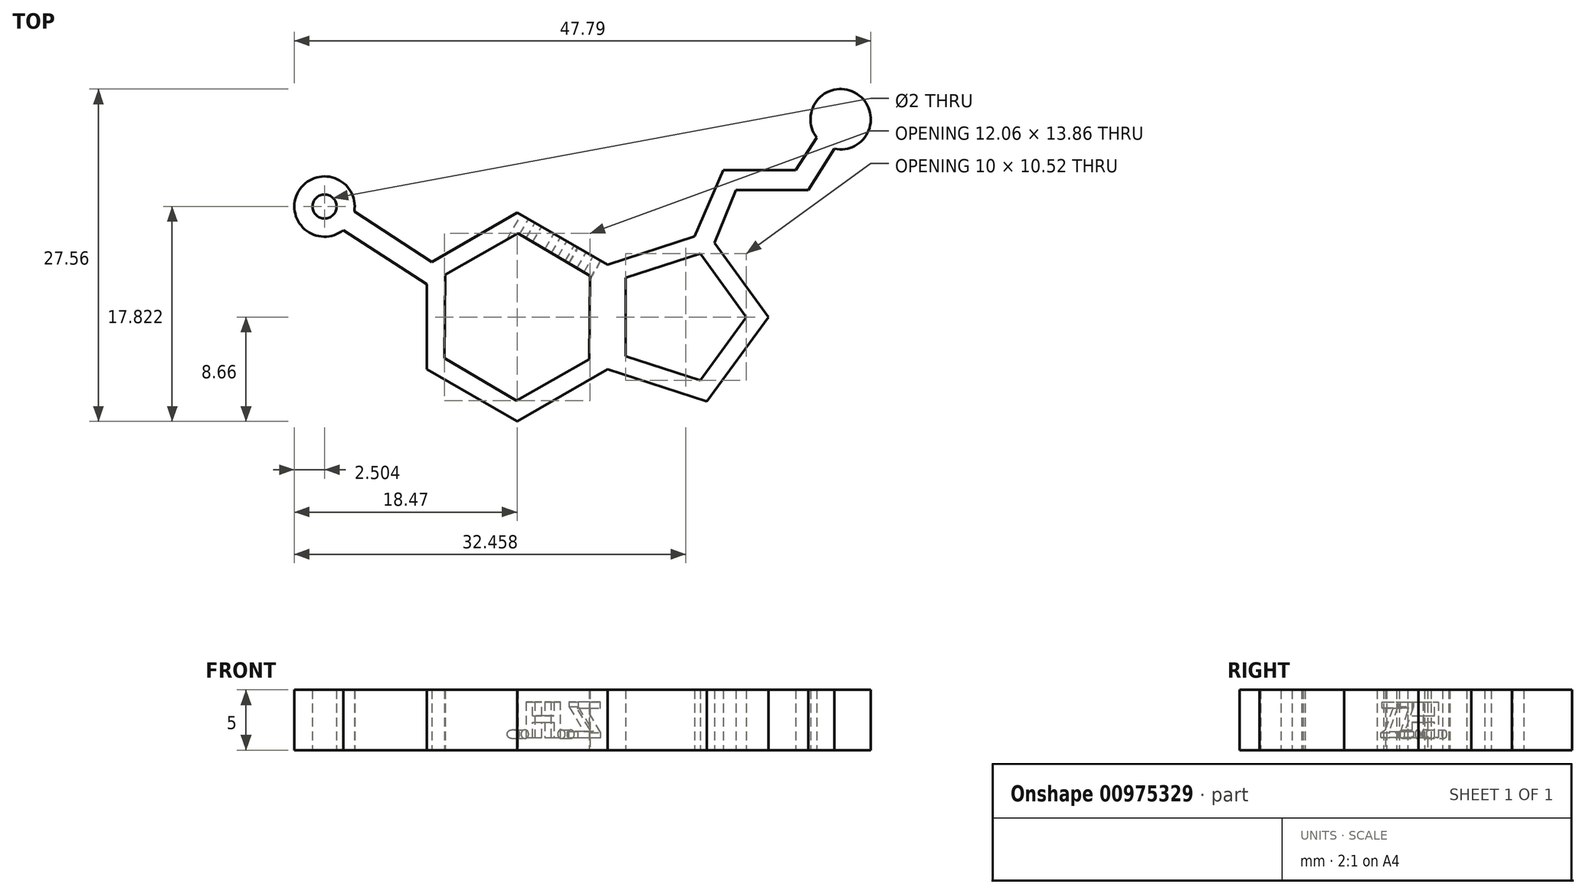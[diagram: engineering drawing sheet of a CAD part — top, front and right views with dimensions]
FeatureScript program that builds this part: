
annotation { "Feature Type Name" : "Feature", "Feature Type Description" : "" }
export const myFeature = defineFeature(function(context is Context, id is Id, definition is map)
    precondition{}
    {
        {
            var Q0;
            Q0=qCreatedBy(makeId("Top.planeOp"),FACE);
            var sketch = newSketch(context, id + "F0", { "sketchPlane" : qUnion([Q0])});
            skCircle(sketch, "E0.cCircle", {"center": v(0, 0) * mm, "radius": 7.5 * mm, "construction": true});
            skLineSegment(sketch, "E0.0", {"start": v(-7.5, 4.33) * mm, "end": v(0, 8.66) * mm});
            skLineSegment(sketch, "E0.1", {"start": v(0, 8.66) * mm, "end": v(7.5, 4.33) * mm});
            skLineSegment(sketch, "E0.2", {"start": v(7.5, 4.33) * mm, "end": v(7.5, -4.33) * mm});
            skLineSegment(sketch, "E0.3", {"start": v(7.5, -4.33) * mm, "end": v(0, -8.66) * mm});
            skLineSegment(sketch, "E0.4", {"start": v(0, -8.66) * mm, "end": v(-7.5, -4.33) * mm});
            skLineSegment(sketch, "E0.5", {"start": v(-7.5, -4.33) * mm, "end": v(-7.5, 4.33) * mm});
            skPoint(sketch, "E0.0.midPoint", {"position": v(-3.75, 6.5) * mm});
            skCircle(sketch, "E1.cCircle", {"center": v(13.46, 0) * mm, "radius": 5.96 * mm, "construction": true});
            skLineSegment(sketch, "E1.0", {"start": v(7.5, 4.33) * mm, "end": v(15.74, 7) * mm});
            skLineSegment(sketch, "E1.1", {"start": v(15.74, 7) * mm, "end": v(20.83, 0) * mm});
            skLineSegment(sketch, "E1.2", {"start": v(20.83, 0) * mm, "end": v(15.74, -7) * mm});
            skLineSegment(sketch, "E1.3", {"start": v(15.74, -7) * mm, "end": v(7.5, -4.33) * mm});
            skLineSegment(sketch, "E1.4", {"start": v(7.5, -4.33) * mm, "end": v(7.5, 4.33) * mm});
            skPoint(sketch, "E1.0.midPoint", {"position": v(11.62, 5.67) * mm});
            skCircle(sketch, "E2.cCircle", {"center": v(0, 0) * mm, "radius": 6 * mm, "construction": true});
            skLineSegment(sketch, "E2.0", {"start": v(0.06, 6.93) * mm, "end": v(6.03, 3.42) * mm});
            skLineSegment(sketch, "E2.1", {"start": v(6.03, 3.42) * mm, "end": v(5.97, -3.51) * mm});
            skLineSegment(sketch, "E2.2", {"start": v(5.97, -3.51) * mm, "end": v(-0.06, -6.93) * mm});
            skLineSegment(sketch, "E2.3", {"start": v(-0.06, -6.93) * mm, "end": v(-6.03, -3.42) * mm});
            skLineSegment(sketch, "E2.4", {"start": v(-6.03, -3.42) * mm, "end": v(-5.97, 3.51) * mm});
            skLineSegment(sketch, "E2.5", {"start": v(-5.97, 3.51) * mm, "end": v(0.06, 6.93) * mm});
            skPoint(sketch, "E2.0.midPoint", {"position": v(3.04, 5.17) * mm});
            skCircle(sketch, "E3.cCircle", {"center": v(13.46, 0) * mm, "radius": 4.47 * mm, "construction": true});
            skLineSegment(sketch, "E3.0", {"start": v(15.17, 5.26) * mm, "end": v(18.99, 0) * mm});
            skLineSegment(sketch, "E3.1", {"start": v(18.99, 0) * mm, "end": v(15.17, -5.26) * mm});
            skLineSegment(sketch, "E3.2", {"start": v(15.17, -5.26) * mm, "end": v(8.99, -3.25) * mm});
            skLineSegment(sketch, "E3.3", {"start": v(8.99, -3.25) * mm, "end": v(8.99, 3.25) * mm});
            skLineSegment(sketch, "E3.4", {"start": v(8.99, 3.25) * mm, "end": v(15.17, 5.26) * mm});
            skPoint(sketch, "E3.0.midPoint", {"position": v(17.08, 2.63) * mm});
            skCircle(sketch, "E4", {"center": v(26.82, 16.4) * mm, "radius": 2.5 * mm});
            skCircle(sketch, "E5", {"center": v(-15.97, 9.16) * mm, "radius": 2.5 * mm});
            skCircle(sketch, "E6", {"center": v(-15.97, 9.16) * mm, "radius": 1 * mm});
            skLineSegment(sketch, "E7", {"start": v(-7.5, 2.71) * mm, "end": v(-15.88, 8.17) * mm});
            skLineSegment(sketch, "E8", {"start": v(-7.08, 4.57) * mm, "end": v(-15.46, 10.02) * mm});
            skLineSegment(sketch, "E9", {"start": v(14.71, 6.67) * mm, "end": v(17.1, 12.18) * mm});
            skLineSegment(sketch, "E10", {"start": v(17.1, 12.18) * mm, "end": v(23.1, 12.18) * mm});
            skLineSegment(sketch, "E11", {"start": v(23.1, 12.18) * mm, "end": v(25.78, 16.4) * mm});
            skLineSegment(sketch, "E12", {"start": v(18.13, 10.52) * mm, "end": v(24.13, 10.52) * mm});
            skLineSegment(sketch, "E13", {"start": v(24.13, 10.52) * mm, "end": v(26.8, 14.74) * mm});
            skLineSegment(sketch, "E14", {"start": v(18.13, 10.52) * mm, "end": v(16.36, 6.15) * mm});
            skSolve(sketch);
        }
        {
            var Q0;
            {var subQ0=sQuery(id+"F0.wireOp",EDGE,"E4");var subQ1=makeQuery(id+"F0.imprint","INTERSECT",VERTEX,{"derivedFrom":[subQ0,sQuery(id+"F0.wireOp",EDGE,"E11")]});Q0=makeQuery(id+"F0.imprint","IMPRINT",FACE,{"disambiguationData":[TD([[makeQuery(id+"F0.imprint","IMPRINT",EDGE,{"disambiguationData":[TD([[subQ1,-1.0]])],"derivedFrom":subQ0}),1.0]])]});}
            var Q1;
            {var subQ0=sQuery(id+"F0.wireOp",EDGE,"E9");Q1=makeQuery(id+"F0.imprint","IMPRINT",FACE,{"disambiguationData":[TD([[makeQuery(id+"F0.imprint","IMPRINT",EDGE,{"derivedFrom":subQ0}),-1.0]])]});}
            var Q2;
            {var subQ6=sQuery(id+"F0.wireOp",EDGE,"E0.1");Q2=makeQuery(id+"F0.imprint","IMPRINT",FACE,{"disambiguationData":[TD([[makeQuery(id+"F0.imprint","IMPRINT",EDGE,{"derivedFrom":subQ6}),-1.0]])]});}
            var Q3;
            {var subQ1=sQuery(id+"F0.wireOp",EDGE,"E1.2");Q3=makeQuery(id+"F0.imprint","IMPRINT",FACE,{"disambiguationData":[TD([[makeQuery(id+"F0.imprint","IMPRINT",EDGE,{"derivedFrom":subQ1}),-1.0]])]});}
            var Q4;
            {var subQ0=sQuery(id+"F0.wireOp",EDGE,"E7");var subQ1=sQuery(id+"F0.wireOp",EDGE,"E5");var subQ2=makeQuery(id+"F0.imprint","INTERSECT",VERTEX,{"derivedFrom":[subQ1,subQ0]});Q4=makeQuery(id+"F0.imprint","IMPRINT",FACE,{"disambiguationData":[TD([[makeQuery(id+"F0.imprint","IMPRINT",EDGE,{"disambiguationData":[TD([[subQ2,-1.0]])],"derivedFrom":subQ1}),1.0]])]});}
            var Q5;
            {var subQ0=sQuery(id+"F0.wireOp",EDGE,"E7");var subQ6=sQuery(id+"F0.wireOp",EDGE,"E5");var subQ7=makeQuery(id+"F0.imprint","INTERSECT",VERTEX,{"derivedFrom":[subQ6,subQ0]});Q5=makeQuery(id+"F0.imprint","IMPRINT",FACE,{"disambiguationData":[TD([[makeQuery(id+"F0.imprint","IMPRINT",EDGE,{"disambiguationData":[TD([[subQ7,1.0]])],"derivedFrom":subQ6}),1.0]])]});}
            var Q6;
            {var subQ1=sQuery(id+"F0.wireOp",EDGE,"E0.5");var subQ7=sQuery(id+"F0.wireOp",EDGE,"E0.0");var subQ8=makeQuery(id+"F0.imprint","INTERSECT",VERTEX,{"derivedFrom":[subQ7,subQ1]});Q6=makeQuery(id+"F0.imprint","IMPRINT",FACE,{"disambiguationData":[TD([[makeQuery(id+"F0.imprint","IMPRINT",EDGE,{"disambiguationData":[TD([[subQ8,-1.0]])],"derivedFrom":subQ7}),1.0]])]});}
            extrude(context, id + "F1", {"entities" : qUnion([Q0, Q1, Q2, Q3, Q4, Q5, Q6]), "depth" : 5 * mm, "offsetDistance" : 25 * mm});
        }
        {
            var Q0;
            Q0=makeQuery(id+"F1.opExtrude","SWEPT_FACE",FACE,{"disambiguationData":[OSD([sQuery(id+"F0.wireOp",EDGE,"E0.1")])]});
            var sketch = newSketch(context, id + "F2", { "sketchPlane" : qUnion([Q0])});
            skText(sketch, "E15", { "text": "Z.H.", "fontName": "OpenSans-Bold.ttf"});
            const initialGuessF2  = {"E15": [-0.00379, 0.00103, 1, 0, 0.003]};
            skSetInitialGuess(sketch, initialGuessF2);
            skSolve(sketch);
        }
        {
            var Q0;
            Q0 = qSketchRegion(id + "F2", true);
            var Q1;
            Q1=makeQuery(id+"F1.opExtrude","SWEPT_FACE",FACE,{"disambiguationData":[OSD([sQuery(id+"F0.wireOp",EDGE,"E0.1")])]});
            extrude(context, id + "F3", {"entities" : qUnion([Q0]), "operationType" : NewBodyOperationType.REMOVE, "oppositeDirection" : true, "depth" : 10 * mm, "endBoundEntityFace" : qUnion([Q1]), "offsetDistance" : 25 * mm});
        }
    });
